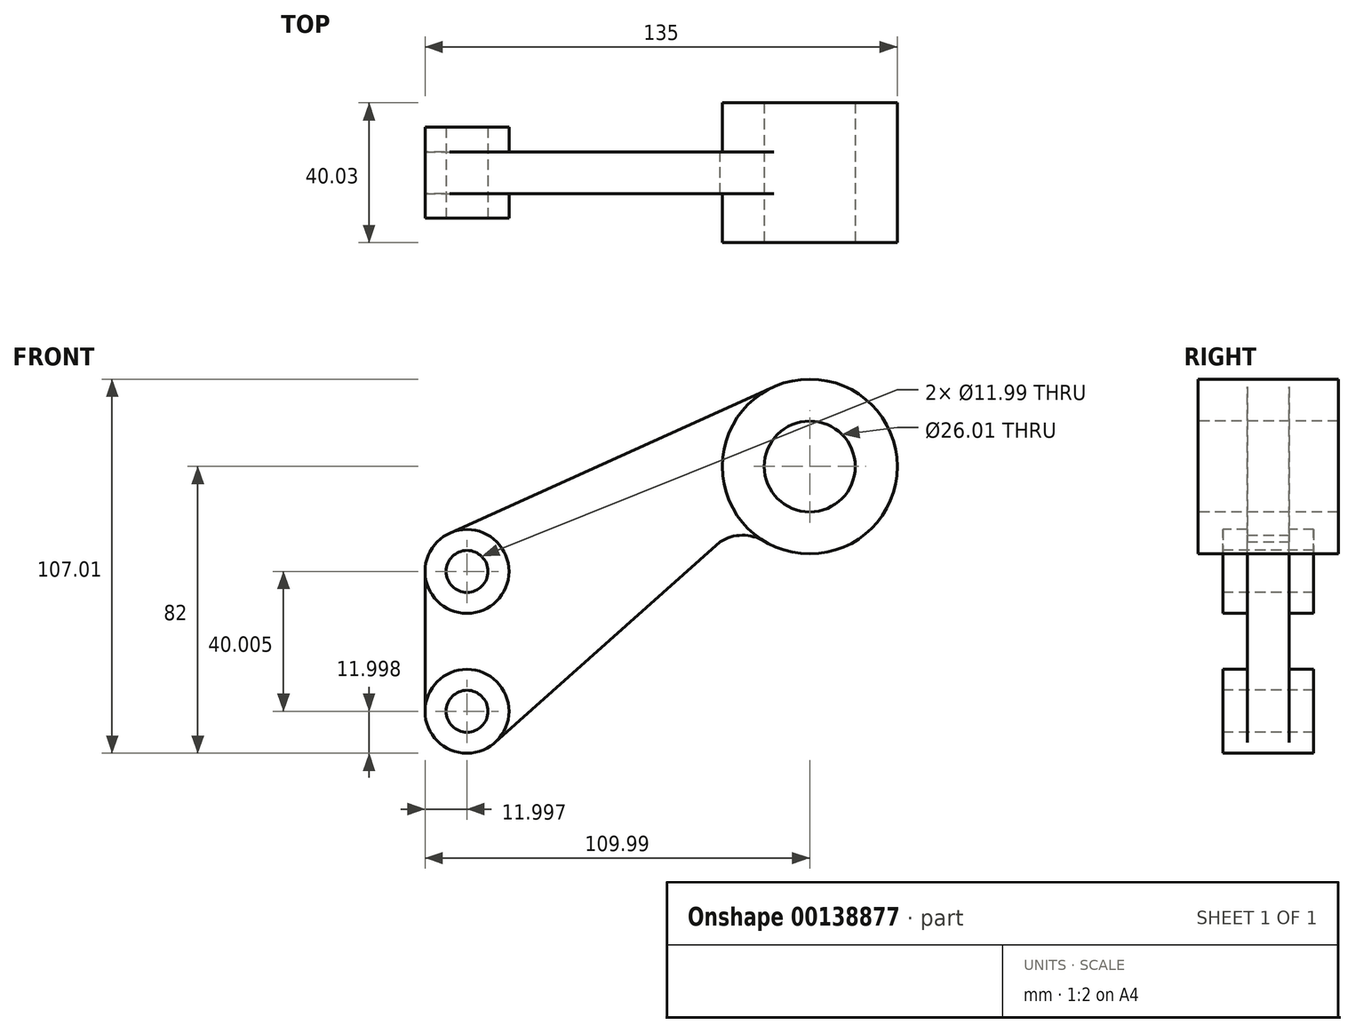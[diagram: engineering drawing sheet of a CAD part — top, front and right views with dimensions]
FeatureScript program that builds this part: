
annotation { "Feature Type Name" : "Feature", "Feature Type Description" : "" }
export const myFeature = defineFeature(function(context is Context, id is Id, definition is map)
    precondition{}
    {
        {
            var Q0;
            Q0=qCreatedBy(makeId("Front.planeOp"),FACE);
            var sketch = newSketch(context, id + "F0", { "sketchPlane" : qUnion([Q0])});
            skCircle(sketch, "E0", {"center": v(-98, -30) * mm, "radius": 6 * mm});
            skCircle(sketch, "E1", {"center": v(-98, -30) * mm, "radius": 12 * mm});
            skCircle(sketch, "E2", {"center": v(-98, -70) * mm, "radius": 12 * mm});
            skCircle(sketch, "E3", {"center": v(-98, -70) * mm, "radius": 6 * mm});
            skCircle(sketch, "E4", {"center": v(0, 0) * mm, "radius": 25 * mm});
            skCircle(sketch, "E5", {"center": v(0, 0) * mm, "radius": 13 * mm});
            skLineSegment(sketch, "E6", {"start": v(-102.93, -19.06) * mm, "end": v(-10.3, 22.79) * mm});
            skLineSegment(sketch, "E7", {"start": v(-110, -70) * mm, "end": v(-110, -30) * mm});
            skLineSegment(sketch, "E8", {"start": v(-90, -78.96) * mm, "end": v(-25.62, -21.55) * mm});
            skArc(sketch, "E9", {"start": v(-12.95, -21.4) * mm, "mid": v(-19.3, -19.66) * mm, "end": v(-25.62, -21.55) * mm});
            skLineSegment(sketch, "E10", {"start": v(-19.16, -31.65) * mm, "end": v(0, 0) * mm, "construction": true});
            skSolve(sketch);
        }
        {
            var Q0;
            {var subQ0=sQuery(id+"F0.wireOp",EDGE,"E6");Q0=makeQuery(id+"F0.imprint","IMPRINT",FACE,{"disambiguationData":[TD([[makeQuery(id+"F0.imprint","IMPRINT",EDGE,{"derivedFrom":subQ0}),-1.0]])]});}
            extrude(context, id + "F1", {"entities" : qUnion([Q0]), "depth" : 12 * mm});
        }
        {
            var Q0;
            Q0=makeQuery(id+"F0.imprint","IMPRINT",FACE,{"disambiguationData":[TD([[makeQuery(id+"F0.imprint","IMPRINT",EDGE,{"derivedFrom":sQuery(id+"F0.wireOp",EDGE,"E0")}),-1.0]])]});
            var Q1;
            Q1=makeQuery(id+"F0.imprint","IMPRINT",FACE,{"disambiguationData":[TD([[makeQuery(id+"F0.imprint","IMPRINT",EDGE,{"derivedFrom":sQuery(id+"F0.wireOp",EDGE,"E3")}),-1.0]])]});
            extrude(context, id + "F2", {"entities" : qUnion([Q0, Q1]), "operationType" : NewBodyOperationType.ADD, "oppositeDirection" : true, "depth" : 7 * mm, "hasSecondDirection" : true, "secondDirectionOppositeDirection" : false, "secondDirectionDepth" : 19 * mm});
        }
        {
            var Q0;
            Q0=makeQuery(id+"F0.imprint","IMPRINT",FACE,{"disambiguationData":[TD([[makeQuery(id+"F0.imprint","IMPRINT",EDGE,{"derivedFrom":sQuery(id+"F0.wireOp",EDGE,"E5")}),-1.0]])]});
            extrude(context, id + "F3", {"entities" : qUnion([Q0]), "operationType" : NewBodyOperationType.ADD, "oppositeDirection" : true, "depth" : 14.02 * mm, "hasSecondDirection" : true, "secondDirectionOppositeDirection" : false, "secondDirectionDepth" : 26 * mm});
        }
    });
